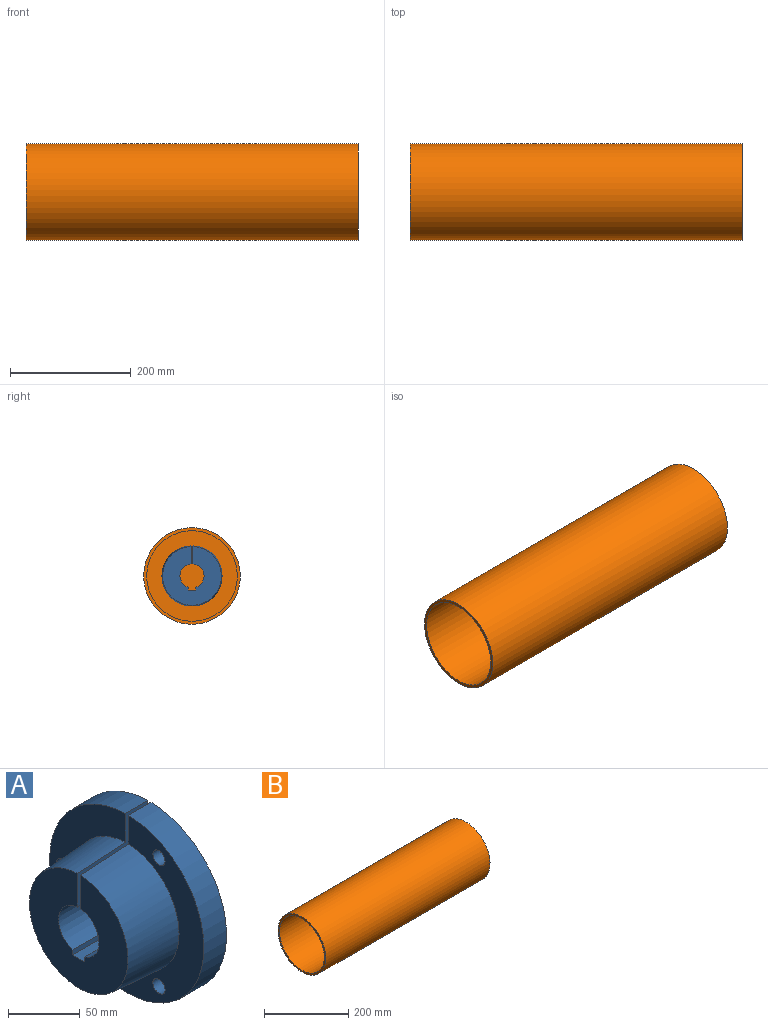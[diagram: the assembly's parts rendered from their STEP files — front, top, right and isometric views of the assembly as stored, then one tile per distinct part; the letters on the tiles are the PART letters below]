
ASSEMBLY  parts=2 mates=1
PART A: 17 faces, bbox 69.9x152.4x152.4 mm
  f0: plane 69.85x56.24mm, normal (0,-1,0), area 2689.6mm2, adj f1,f9,f11,f12,f13,f14,f16
  f1: cylinder r=20mm len=39.02mm, axis (1,0,0), area 1234.6mm2, adj f0,f2,f12,f14
  f2: plane 69.85x4.22mm, normal (0,-1,0), area 294.9mm2, adj f1,f3,f12,f13,f14
  f3: plane 69.85x12mm, normal (0,0,1), area 838.2mm2, adj f2,f4,f12,f13
  f4: plane 69.85x4.22mm, normal (0,1,0), area 294.9mm2, adj f3,f5,f12,f13,f15
  f5: cylinder r=20mm len=39.02mm, axis (1,0,0), area 1234.6mm2, adj f4,f6,f12,f15
  f6: plane 69.85x56.24mm, normal (0,1,0), area 2689.6mm2, adj f5,f9,f11,f12,f13,f15,f16
  f7: cylinder r=6mm len=22.35mm, axis (1,0,0), area 842.7mm2, adj f11,f12
  f8: cylinder r=6mm len=22.35mm, axis (1,0,0), area 842.7mm2, adj f11,f12
  f9: cylinder r=76.2mm len=152.4mm, axis (1,0,0), area 10634.6mm2, adj f0,f6,f11,f12
  f10: cylinder r=6mm len=22.35mm, axis (1,0,0), area 842.7mm2, adj f11,f12
  f11: plane 152.4x152.39mm, normal (-1,0,0), area 9461.5mm2, adj f0,f6,f7,f8,f9,f10,f16
  f12: plane 152.4x152.39mm, normal (1,0,0), area 16433.6mm2, adj f0,f1,f2,f3,f4,f5,f6,f7
  f13: plane 97.32x97.26mm, normal (-1,0,0), area 6046.6mm2, adj f0,f2,f3,f4,f6,f14,f15,f16
  f14: cone r=20mm half-angle=0deg, axis (-1,0,0), area 2623.6mm2, adj f0,f1,f2,f13
  f15: cone r=20mm half-angle=0deg, axis (-1,0,0), area 2623.6mm2, adj f4,f5,f6,f13
  f16: bspline ~103.2x103.09mm, area 14845.7mm2, adj f0,f6,f11,f13
PART B: 7 faces, bbox 550x160x160 mm
  f0: cylinder r=75mm len=498.13mm, axis (1,0,0), area 234735.9mm2, adj f3,f6
  f1: cylinder r=75mm len=150mm, axis (1,0,0), area 16964.6mm2, adj f4,f5
  f2: cylinder r=80mm len=550mm, axis (1,0,0), area 276460.2mm2, adj f3,f4
  f3: plane 160x160mm, normal (-1,0,0), area 2434.7mm2, adj f0,f2
  f4: plane 160x160mm, normal (1,0,0), area 2434.7mm2, adj f1,f2
  f5: plane 150x150mm, normal (1,0,0), area 17671.5mm2, adj f1
  f6: plane 150x150mm, normal (-1,0,0), area 17671.5mm2, adj f0
PLACE A t=(97.74,-85.93,81.53)mm
PLACE B t=(111.39,-54.75,59.57)mm
MATE parallel A.f1 <-> B.f0  axis (-1,0,0) through (75.39,-54.75,59.57)mm
